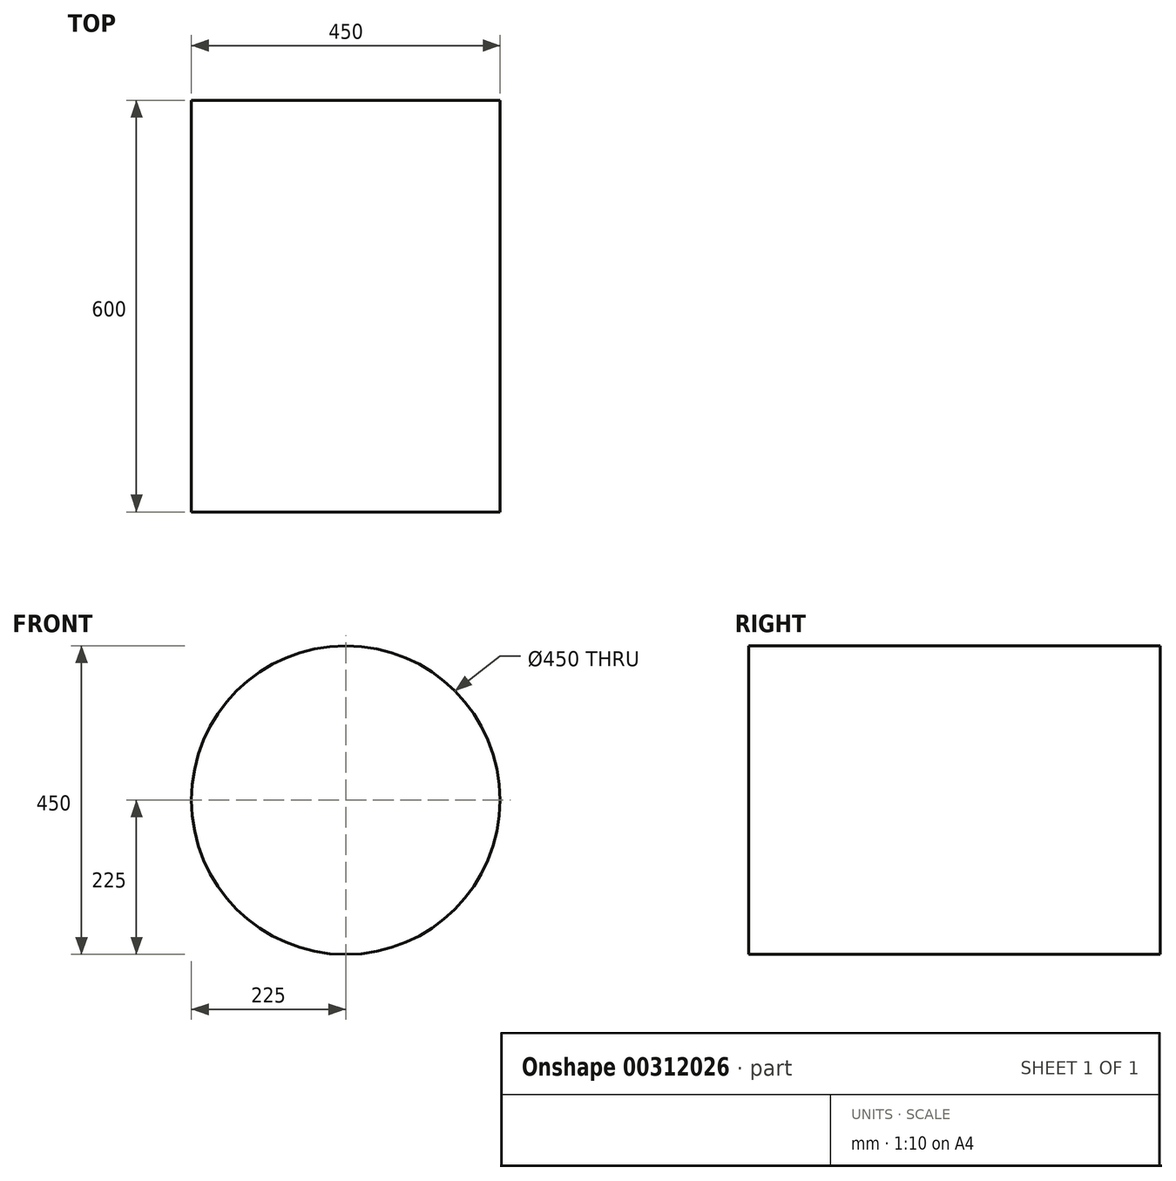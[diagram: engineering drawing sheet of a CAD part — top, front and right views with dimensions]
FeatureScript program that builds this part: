
annotation { "Feature Type Name" : "Feature", "Feature Type Description" : "" }
export const myFeature = defineFeature(function(context is Context, id is Id, definition is map)
    precondition{}
    {
        {
            var Q0;
            Q0=qCreatedBy(makeId("Front.planeOp"),FACE);
            var sketch = newSketch(context, id + "F0", { "sketchPlane" : qUnion([Q0])});
            skCircle(sketch, "E0", {"center": v(0, 0) * mm, "radius": 225 * mm});
            skSolve(sketch);
        }
        {
            var Q0;
            Q0=sQuery(id+"F0.wireOp",EDGE,"E0");
            extrude(context, id + "F1", {"bodyType" : ToolBodyType.SURFACE, "surfaceEntities" : qUnion([Q0]), "oppositeDirection" : true, "depth" : 600 * mm});
        }
    });
